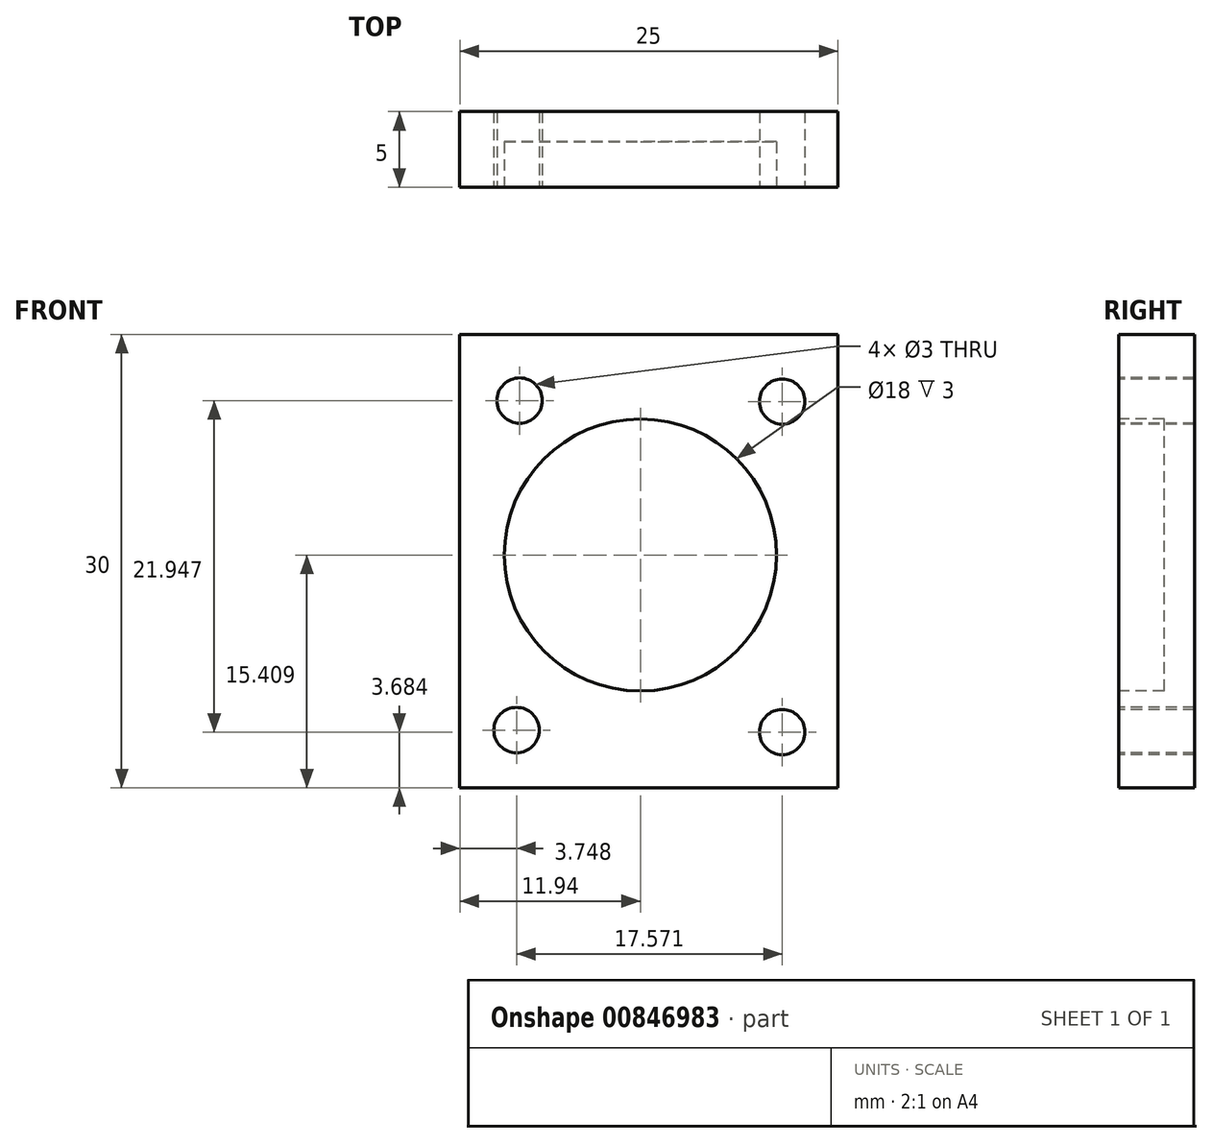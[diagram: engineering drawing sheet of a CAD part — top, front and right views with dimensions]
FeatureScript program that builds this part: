
annotation { "Feature Type Name" : "Feature", "Feature Type Description" : "" }
export const myFeature = defineFeature(function(context is Context, id is Id, definition is map)
    precondition{}
    {
        {
            var Q0;
            Q0=qCreatedBy(makeId("Front.planeOp"),FACE);
            var sketch = newSketch(context, id + "F0", { "sketchPlane" : qUnion([Q0])});
            skLineSegment(sketch, "E0.bottom", {"start": v(-11.94, 17.6) * mm, "end": v(13.06, 17.6) * mm});
            skLineSegment(sketch, "E0.top", {"start": v(-11.94, -12.4) * mm, "end": v(13.06, -12.4) * mm});
            skLineSegment(sketch, "E0.left", {"start": v(-11.94, 17.6) * mm, "end": v(-11.94, -12.4) * mm});
            skLineSegment(sketch, "E0.right", {"start": v(13.06, 17.6) * mm, "end": v(13.06, -12.4) * mm});
            skSolve(sketch);
        }
        {
            var Q0;
            Q0=makeQuery(id+"F0.imprint","IMPRINT",FACE,{"disambiguationData":[TD([[makeQuery(id+"F0.imprint","IMPRINT",EDGE,{"derivedFrom":sQuery(id+"F0.wireOp",EDGE,"E0.bottom")}),-1.0]])]});
            extrude(context, id + "F1", {"entities" : qUnion([Q0]), "depth" : 5 * mm, "offsetDistance" : 25 * mm});
        }
        {
            var Q0;
            Q0=makeQuery(id+"F1.opExtrude","CAP_FACE",FACE,{"disambiguationData":[OSD([sQuery(id+"F0.wireOp",EDGE,"E0.bottom"),sQuery(id+"F0.wireOp",EDGE,"E0.top"),sQuery(id+"F0.wireOp",EDGE,"E0.left"),sQuery(id+"F0.wireOp",EDGE,"E0.right")])],"isStart":false});
            var sketch = newSketch(context, id + "F2", { "sketchPlane" : qUnion([Q0])});
            skCircle(sketch, "E1", {"center": v(-7.99, 13.23) * mm, "radius": 1.5 * mm});
            skCircle(sketch, "E2", {"center": v(9.38, 13.16) * mm, "radius": 1.5 * mm});
            skCircle(sketch, "E3", {"center": v(-8.2, -8.58) * mm, "radius": 1.5 * mm});
            skCircle(sketch, "E4", {"center": v(9.38, -8.72) * mm, "radius": 1.5 * mm});
            skCircle(sketch, "E5", {"center": v(0, 2.22) * mm, "radius": 9 * mm});
            skSolve(sketch);
        }
        {
            var Q0;
            Q0=makeQuery(id+"F2.imprint","IMPRINT",FACE,{"disambiguationData":[TD([[makeQuery(id+"F2.imprint","IMPRINT",EDGE,{"derivedFrom":sQuery(id+"F2.wireOp",EDGE,"E1")}),1.0]])]});
            var Q1;
            Q1=makeQuery(id+"F2.imprint","IMPRINT",FACE,{"disambiguationData":[TD([[makeQuery(id+"F2.imprint","IMPRINT",EDGE,{"derivedFrom":sQuery(id+"F2.wireOp",EDGE,"E2")}),1.0]])]});
            var Q2;
            Q2=makeQuery(id+"F2.imprint","IMPRINT",FACE,{"disambiguationData":[TD([[makeQuery(id+"F2.imprint","IMPRINT",EDGE,{"derivedFrom":sQuery(id+"F2.wireOp",EDGE,"E3")}),1.0]])]});
            var Q3;
            Q3=makeQuery(id+"F2.imprint","IMPRINT",FACE,{"disambiguationData":[TD([[makeQuery(id+"F2.imprint","IMPRINT",EDGE,{"derivedFrom":sQuery(id+"F2.wireOp",EDGE,"E4")}),1.0]])]});
            extrude(context, id + "F3", {"entities" : qUnion([Q0, Q1, Q2, Q3]), "operationType" : NewBodyOperationType.REMOVE, "oppositeDirection" : true, "depth" : 25 * mm, "offsetDistance" : 25 * mm});
        }
        {
            var Q0;
            Q0=makeQuery(id+"F1.opExtrude","CAP_FACE",FACE,{"disambiguationData":[OSD([sQuery(id+"F0.wireOp",EDGE,"E0.bottom"),sQuery(id+"F0.wireOp",EDGE,"E0.top"),sQuery(id+"F0.wireOp",EDGE,"E0.left"),sQuery(id+"F0.wireOp",EDGE,"E0.right")])],"isStart":false});
            var sketch = newSketch(context, id + "F4", { "sketchPlane" : qUnion([Q0])});
            skCircle(sketch, "E6", {"center": v(0, 3) * mm, "radius": 9 * mm});
            skSolve(sketch);
        }
        {
            var Q0;
            Q0=makeQuery(id+"F4.imprint","IMPRINT",FACE,{"disambiguationData":[TD([[makeQuery(id+"F4.imprint","IMPRINT",EDGE,{"derivedFrom":sQuery(id+"F4.wireOp",EDGE,"E6")}),1.0]])]});
            extrude(context, id + "F5", {"entities" : qUnion([Q0]), "operationType" : NewBodyOperationType.REMOVE, "oppositeDirection" : true, "depth" : 3 * mm, "offsetDistance" : 25 * mm});
        }
    });
